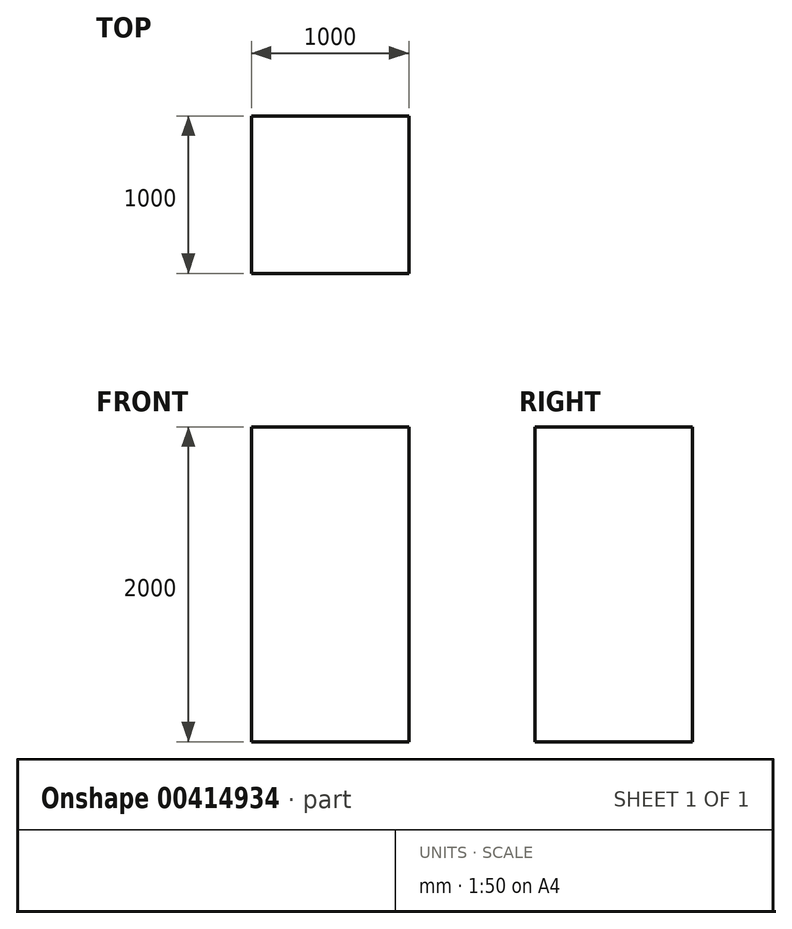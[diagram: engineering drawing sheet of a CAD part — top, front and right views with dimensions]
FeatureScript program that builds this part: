
annotation { "Feature Type Name" : "Feature", "Feature Type Description" : "" }
export const myFeature = defineFeature(function(context is Context, id is Id, definition is map)
    precondition{}
    {
        {
            var Q0;
            Q0=qCreatedBy(makeId("Top.planeOp"),FACE);
            var sketch = newSketch(context, id + "F0", { "sketchPlane" : qUnion([Q0])});
            skLineSegment(sketch, "E0.bottom", {"start": v(0, 0) * mm, "end": v(1000, 0) * mm});
            skLineSegment(sketch, "E0.top", {"start": v(0, 1000) * mm, "end": v(1000, 1000) * mm});
            skLineSegment(sketch, "E0.left", {"start": v(0, 0) * mm, "end": v(0, 1000) * mm});
            skLineSegment(sketch, "E0.right", {"start": v(1000, 0) * mm, "end": v(1000, 1000) * mm});
            skSolve(sketch);
        }
        {
            var Q0;
            Q0 = qSketchRegion(id + "F0", true);
            extrude(context, id + "F1", {"entities" : qUnion([Q0]), "depth" : 2000 * mm});
        }
    });
